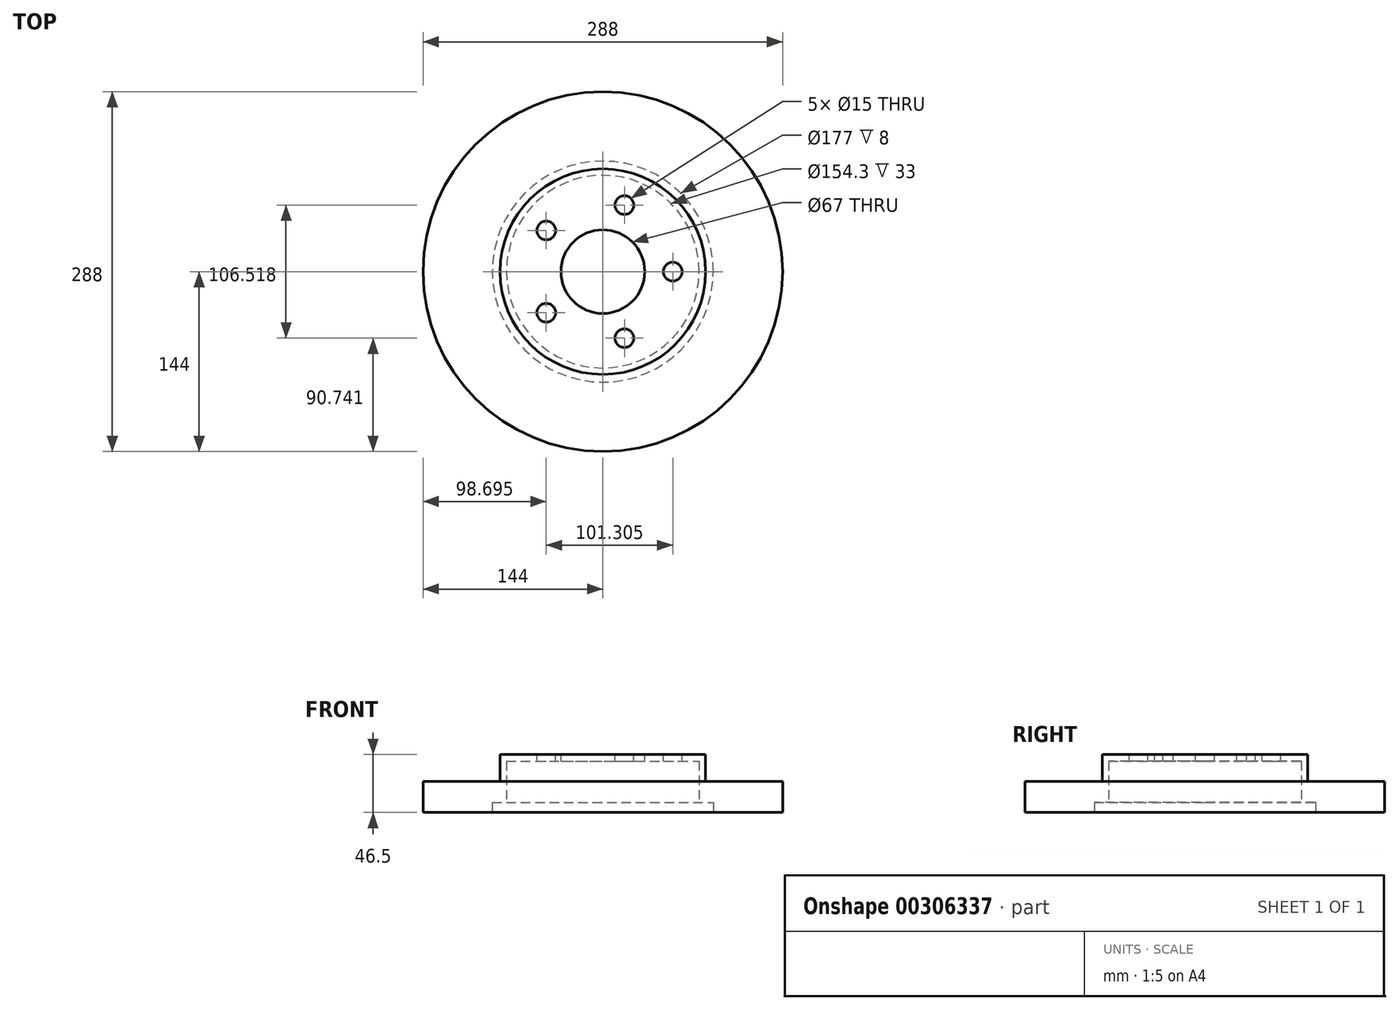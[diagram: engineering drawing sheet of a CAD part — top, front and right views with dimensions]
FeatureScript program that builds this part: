
annotation { "Feature Type Name" : "Feature", "Feature Type Description" : "" }
export const myFeature = defineFeature(function(context is Context, id is Id, definition is map)
    precondition{}
    {
        {
            var Q0;
            Q0=qCreatedBy(makeId("Top.planeOp"),FACE);
            var sketch = newSketch(context, id + "F0", { "sketchPlane" : qUnion([Q0])});
            skCircle(sketch, "E0", {"center": v(0, 0) * mm, "radius": 144 * mm});
            skSolve(sketch);
        }
        {
            var Q0;
            Q0 = qSketchRegion(id + "F0", true);
            extrude(context, id + "F1", {"entities" : qUnion([Q0]), "depth" : 25 * mm});
        }
        {
            var Q0;
            Q0=makeQuery(id+"F1.opExtrude","CAP_FACE",FACE,{"disambiguationData":[OSD([sQuery(id+"F0.wireOp",EDGE,"E0")])],"isStart":false});
            var sketch = newSketch(context, id + "F2", { "sketchPlane" : qUnion([Q0])});
            skCircle(sketch, "E1", {"center": v(0, 0) * mm, "radius": 82.3 * mm});
            skSolve(sketch);
        }
        {
            var Q0;
            Q0 = qSketchRegion(id + "F2", true);
            extrude(context, id + "F3", {"entities" : qUnion([Q0]), "operationType" : NewBodyOperationType.ADD, "depth" : 21.5 * mm});
        }
        {
            var Q0;
            Q0=makeQuery(id+"F1.opExtrude","CAP_FACE",FACE,{"disambiguationData":[OSD([sQuery(id+"F0.wireOp",EDGE,"E0")])],"isStart":true});
            var sketch = newSketch(context, id + "F4", { "sketchPlane" : qUnion([Q0])});
            skCircle(sketch, "E2", {"center": v(0, 0) * mm, "radius": 77.15 * mm});
            skSolve(sketch);
        }
        {
            var Q0;
            Q0 = qSketchRegion(id + "F4", true);
            extrude(context, id + "F5", {"entities" : qUnion([Q0]), "operationType" : NewBodyOperationType.REMOVE, "oppositeDirection" : true, "depth" : 41 * mm});
        }
        {
            var Q0;
            Q0=makeQuery(id+"F1.opExtrude","CAP_FACE",FACE,{"disambiguationData":[OSD([sQuery(id+"F0.wireOp",EDGE,"E0")])],"isStart":true});
            var sketch = newSketch(context, id + "F6", { "sketchPlane" : qUnion([Q0])});
            skCircle(sketch, "E3", {"center": v(0, 0) * mm, "radius": 88.5 * mm});
            skSolve(sketch);
        }
        {
            var Q0;
            Q0 = qSketchRegion(id + "F6", true);
            extrude(context, id + "F7", {"entities" : qUnion([Q0]), "operationType" : NewBodyOperationType.REMOVE, "oppositeDirection" : true, "depth" : 8 * mm});
        }
        {
            var Q0;
            Q0=makeQuery(id+"F3.opExtrude","CAP_FACE",FACE,{"disambiguationData":[OSD([sQuery(id+"F2.wireOp",EDGE,"E1")])],"isStart":false});
            var sketch = newSketch(context, id + "F8", { "sketchPlane" : qUnion([Q0])});
            skCircle(sketch, "E4", {"center": v(0, 0) * mm, "radius": 33.5 * mm});
            skCircle(sketch, "E5", {"center": v(56, 0) * mm, "radius": 7.5 * mm});
            skCircle(sketch, "E6.1.0", {"center": v(17.3, 53.26) * mm, "radius": 7.5 * mm});
            skCircle(sketch, "E6.2.0", {"center": v(-45.3, 32.92) * mm, "radius": 7.5 * mm});
            skCircle(sketch, "E6.3.0", {"center": v(-45.3, -32.92) * mm, "radius": 7.5 * mm});
            skCircle(sketch, "E6.4.0", {"center": v(17.3, -53.26) * mm, "radius": 7.5 * mm});
            skSolve(sketch);
        }
        {
            var Q0;
            Q0 = qSketchRegion(id + "F8", true);
            extrude(context, id + "F9", {"entities" : qUnion([Q0]), "operationType" : NewBodyOperationType.REMOVE, "oppositeDirection" : true, "depth" : 25 * mm});
        }
    });
